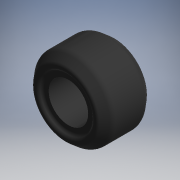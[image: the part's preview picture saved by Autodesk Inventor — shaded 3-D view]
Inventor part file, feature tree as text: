
AUTODESK INVENTOR PART (.ipt)
format: ipt  version: 2016 (Build 200138000, 138)  size: 143,360 bytes
history: native  units: mm (DEFAULTED — no unit token found)
features: fillet x1
ambient origin geometry x8: Origin, YZ Plane, XZ Plane, XY Plane, X Axis, Y Axis, Z Axis, Center Point
bodies: Solid1 (feature_tree)
feature tree (1):
  fillet  "Fillet3"  [1 undecoded]
note: 1 required parameter value undecoded (feature->parameter linkage not recoverable at this tier; creation-order binding heuristic only, values carry confidence <= 0.55)
